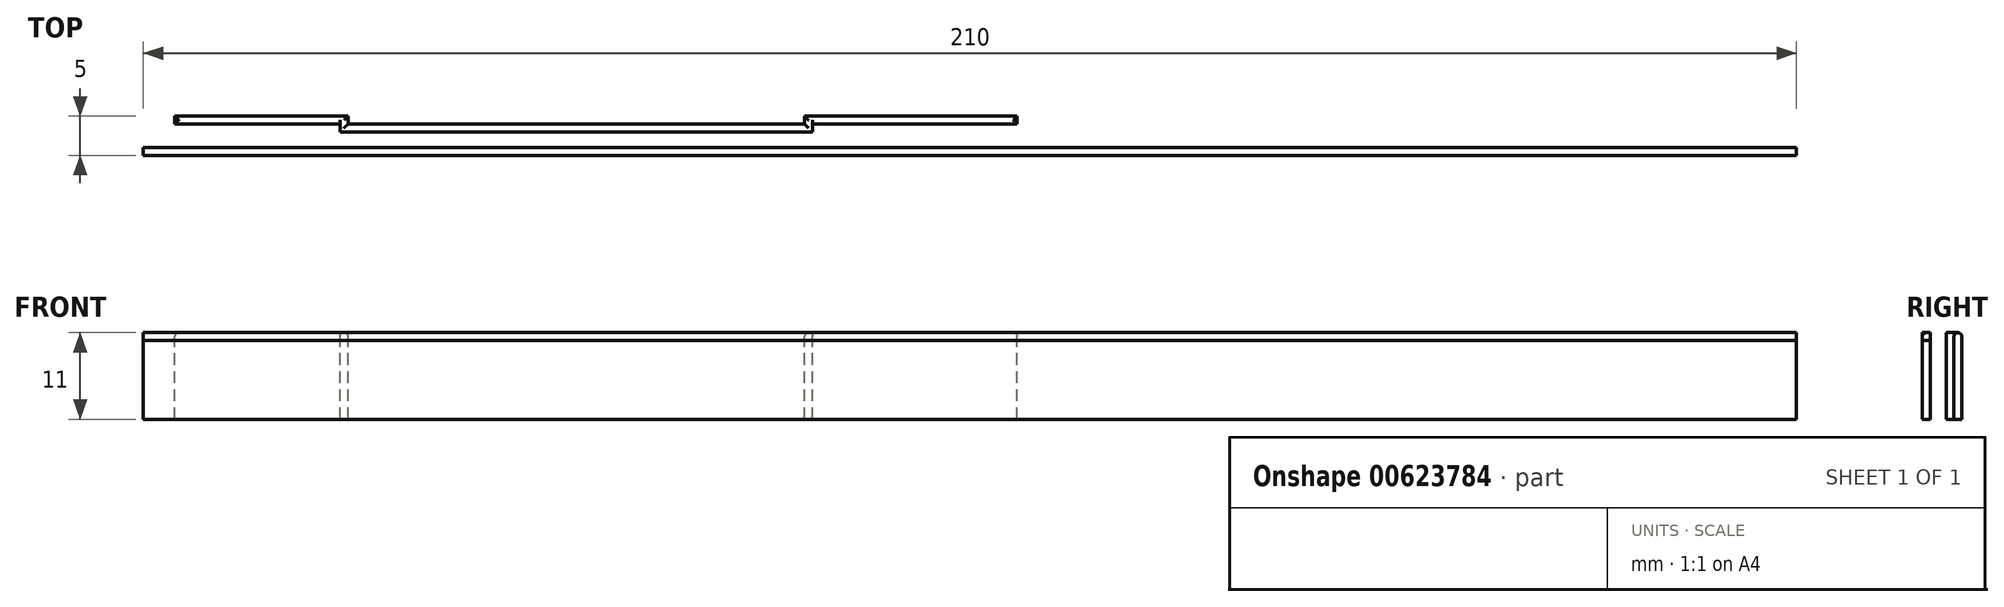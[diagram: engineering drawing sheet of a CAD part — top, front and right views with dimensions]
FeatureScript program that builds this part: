
annotation { "Feature Type Name" : "Feature", "Feature Type Description" : "" }
export const myFeature = defineFeature(function(context is Context, id is Id, definition is map)
    precondition{}
    {
        {
            var Q0;
            Q0=qCreatedBy(makeId("Top.planeOp"),FACE);
            var sketch = newSketch(context, id + "F0", { "sketchPlane" : qUnion([Q0])});
            skLineSegment(sketch, "E0.bottom", {"start": v(-105, -5) * mm, "end": v(105, -5) * mm});
            skLineSegment(sketch, "E0.top", {"start": v(-105, -9) * mm, "end": v(105, -9) * mm});
            skLineSegment(sketch, "E0.left", {"start": v(-105, -5) * mm, "end": v(-105, -9) * mm});
            skLineSegment(sketch, "E0.right", {"start": v(105, -5) * mm, "end": v(105, -9) * mm});
            skLineSegment(sketch, "E1", {"start": v(0, 0) * mm, "end": v(0, -5) * mm, "construction": true});
            skLineSegment(sketch, "E2", {"start": v(0, -5) * mm, "end": v(105, -5) * mm, "construction": true});
            skLineSegment(sketch, "E3.left", {"start": v(-105, -5) * mm, "end": v(-105, -5) * mm});
            skLineSegment(sketch, "E3.right", {"start": v(105, -5) * mm, "end": v(105, -5) * mm});
            skLineSegment(sketch, "E4.top", {"start": v(-105, -6) * mm, "end": v(105, -6) * mm});
            skLineSegment(sketch, "E4.left", {"start": v(-105, -5) * mm, "end": v(-105, -6) * mm});
            skLineSegment(sketch, "E4.right", {"start": v(105, -5) * mm, "end": v(105, -6) * mm});
            skLineSegment(sketch, "E5.top", {"start": v(-105, -8) * mm, "end": v(105, -8) * mm});
            skLineSegment(sketch, "E5.left", {"start": v(-105, -9) * mm, "end": v(-105, -8) * mm});
            skLineSegment(sketch, "E5.right", {"start": v(105, -9) * mm, "end": v(105, -8) * mm});
            skLineSegment(sketch, "E6", {"start": v(-105, -6) * mm, "end": v(-100, -6) * mm, "construction": true});
            skLineSegment(sketch, "E7", {"start": v(-100, -6) * mm, "end": v(-80, -6) * mm, "construction": true});
            skLineSegment(sketch, "E8", {"start": v(-80, -6) * mm, "end": v(-20, -6) * mm, "construction": true});
            skLineSegment(sketch, "E9", {"start": v(-20, -6) * mm, "end": v(5, -6) * mm, "construction": true});
            skLineSegment(sketch, "E10.bottom", {"start": v(-100, -6) * mm, "end": v(-80, -6) * mm});
            skLineSegment(sketch, "E10.top", {"start": v(-100, -5) * mm, "end": v(-80, -5) * mm});
            skLineSegment(sketch, "E10.left", {"start": v(-100, -6) * mm, "end": v(-100, -5) * mm});
            skLineSegment(sketch, "E10.right", {"start": v(-80, -6) * mm, "end": v(-80, -5) * mm});
            skLineSegment(sketch, "E11.bottom", {"start": v(-101, -5) * mm, "end": v(-79, -5) * mm});
            skLineSegment(sketch, "E11.top", {"start": v(-101, -4) * mm, "end": v(-79, -4) * mm});
            skLineSegment(sketch, "E11.left", {"start": v(-101, -5) * mm, "end": v(-101, -4) * mm});
            skLineSegment(sketch, "E11.right", {"start": v(-79, -5) * mm, "end": v(-79, -4) * mm});
            skLineSegment(sketch, "E12", {"start": v(-101, -5) * mm, "end": v(-100, -5) * mm});
            skLineSegment(sketch, "E13.bottom", {"start": v(-20, -6) * mm, "end": v(5, -6) * mm});
            skLineSegment(sketch, "E13.top", {"start": v(-20, -5) * mm, "end": v(5, -5) * mm});
            skLineSegment(sketch, "E13.left", {"start": v(-20, -6) * mm, "end": v(-20, -5) * mm});
            skLineSegment(sketch, "E13.right", {"start": v(5, -6) * mm, "end": v(5, -5) * mm});
            skLineSegment(sketch, "E14.bottom", {"start": v(-21, -5) * mm, "end": v(6, -5) * mm});
            skLineSegment(sketch, "E14.top", {"start": v(-21, -4) * mm, "end": v(6, -4) * mm});
            skLineSegment(sketch, "E14.left", {"start": v(-21, -5) * mm, "end": v(-21, -4) * mm});
            skLineSegment(sketch, "E14.right", {"start": v(6, -5) * mm, "end": v(6, -4) * mm});
            skLineSegment(sketch, "E15", {"start": v(-21, -5) * mm, "end": v(-20, -5) * mm, "construction": true});
            skSolve(sketch);
        }
        {
            var Q0;
            {var subQ4=sQuery(id+"F0.wireOp",EDGE,"E0.left");Q0=makeQuery(id+"F0.imprint","IMPRINT",FACE,{"disambiguationData":[TD([[makeQuery(id+"F0.imprint","IMPRINT",EDGE,{"derivedFrom":subQ4}),1.0]])]});}
            var Q1;
            Q1=makeQuery(id+"F0.imprint","IMPRINT",FACE,{"disambiguationData":[TD([[makeQuery(id+"F0.imprint","IMPRINT",EDGE,{"derivedFrom":sQuery(id+"F0.wireOp",EDGE,"E10.bottom")}),1.0]])]});
            var Q2;
            Q2=makeQuery(id+"F0.imprint","IMPRINT",FACE,{"disambiguationData":[TD([[makeQuery(id+"F0.imprint","IMPRINT",EDGE,{"derivedFrom":sQuery(id+"F0.wireOp",EDGE,"E13.bottom")}),1.0]])]});
            extrude(context, id + "F1", {"entities" : qUnion([Q0, Q1, Q2]), "oppositeDirection" : true, "depth" : 1 * mm, "offsetDistance" : 25 * mm});
        }
        {
            var Q0;
            Q0=makeQuery(id+"F0.imprint","IMPRINT",FACE,{"disambiguationData":[TD([[makeQuery(id+"F0.imprint","IMPRINT",EDGE,{"derivedFrom":sQuery(id+"F0.wireOp",EDGE,"E11.top")}),-1.0]])]});
            var Q1;
            {var subQ0=sQuery(id+"F0.wireOp",EDGE,"E4.left");Q1=makeQuery(id+"F0.imprint","IMPRINT",FACE,{"disambiguationData":[TD([[makeQuery(id+"F0.imprint","IMPRINT",EDGE,{"derivedFrom":subQ0}),1.0]])]});}
            var Q2;
            {var subQ0=sQuery(id+"F0.wireOp",EDGE,"E10.right");Q2=makeQuery(id+"F0.imprint","IMPRINT",FACE,{"disambiguationData":[TD([[makeQuery(id+"F0.imprint","IMPRINT",EDGE,{"derivedFrom":subQ0}),-1.0]])]});}
            var Q3;
            Q3=makeQuery(id+"F0.imprint","IMPRINT",FACE,{"disambiguationData":[TD([[makeQuery(id+"F0.imprint","IMPRINT",EDGE,{"derivedFrom":sQuery(id+"F0.wireOp",EDGE,"E0.top")}),1.0]])]});
            var Q4;
            Q4=makeQuery(id+"F0.imprint","IMPRINT",FACE,{"disambiguationData":[TD([[makeQuery(id+"F0.imprint","IMPRINT",EDGE,{"derivedFrom":sQuery(id+"F0.wireOp",EDGE,"E14.top")}),-1.0]])]});
            var Q5;
            {var subQ1=sQuery(id+"F0.wireOp",EDGE,"E4.right");Q5=makeQuery(id+"F0.imprint","IMPRINT",FACE,{"disambiguationData":[TD([[makeQuery(id+"F0.imprint","IMPRINT",EDGE,{"derivedFrom":subQ1}),-1.0]])]});}
            extrude(context, id + "F2", {"entities" : qUnion([Q0, Q1, Q2, Q3, Q4, Q5]), "oppositeDirection" : true, "depth" : 11 * mm, "offsetDistance" : 25 * mm});
        }
        {
            var Q0;
            {var subQ0=sQuery(id+"F0.wireOp",EDGE,"E0.bottom");Q0=makeQuery(id+"F2.opExtrude","CAP_EDGE",EDGE,{"disambiguationData":[OSD([subQ0]),TDD([makeQuery(id+"F0.imprint","IMPRINT",EDGE,{"disambiguationData":[TD([[makeQuery(id+"F0.imprint","INTERSECT",VERTEX,{"derivedFrom":[subQ0,sQuery(id+"F0.wireOp",EDGE,"E11.bottom"),sQuery(id+"F0.wireOp",EDGE,"E11.right")]}),-1.0]])],"derivedFrom":subQ0})])],"isStart":true});}
            var Q1;
            Q1=makeQuery(id+"F2.opExtrude","CAP_EDGE",EDGE,{"disambiguationData":[OSD([sQuery(id+"F0.wireOp",EDGE,"E14.left")])],"isStart":true});
            var Q2;
            Q2=makeQuery(id+"F2.opExtrude","CAP_EDGE",EDGE,{"disambiguationData":[OSD([sQuery(id+"F0.wireOp",EDGE,"E14.top")])],"isStart":true});
            var Q3;
            Q3=makeQuery(id+"F2.opExtrude","CAP_EDGE",EDGE,{"disambiguationData":[OSD([sQuery(id+"F0.wireOp",EDGE,"E0.top")])],"isStart":true});
            var Q4;
            Q4=makeQuery(id+"F2.opExtrude","CAP_EDGE",EDGE,{"disambiguationData":[OSD([sQuery(id+"F0.wireOp",EDGE,"E14.right")])],"isStart":true});
            var Q5;
            {var subQ0=sQuery(id+"F0.wireOp",EDGE,"E0.bottom");Q5=makeQuery(id+"F2.opExtrude","CAP_EDGE",EDGE,{"disambiguationData":[OSD([subQ0]),TDD([makeQuery(id+"F0.imprint","IMPRINT",EDGE,{"disambiguationData":[TD([[makeQuery(id+"F0.imprint","INTERSECT",VERTEX,{"derivedFrom":[subQ0,sQuery(id+"F0.wireOp",EDGE,"E4.right")]}),1.0]])],"derivedFrom":subQ0})])],"isStart":true});}
            var Q6;
            Q6=makeQuery(id+"F2.opExtrude","CAP_EDGE",EDGE,{"disambiguationData":[OSD([sQuery(id+"F0.wireOp",EDGE,"E11.top")])],"isStart":true});
            var Q7;
            Q7=makeQuery(id+"F2.opExtrude","CAP_EDGE",EDGE,{"disambiguationData":[OSD([sQuery(id+"F0.wireOp",EDGE,"E11.right")])],"isStart":true});
            var Q8;
            Q8=makeQuery(id+"F2.opExtrude","CAP_EDGE",EDGE,{"disambiguationData":[OSD([sQuery(id+"F0.wireOp",EDGE,"E11.left")])],"isStart":true});
            var Q9;
            {var subQ0=sQuery(id+"F0.wireOp",EDGE,"E0.bottom");Q9=makeQuery(id+"F2.opExtrude","CAP_EDGE",EDGE,{"disambiguationData":[OSD([subQ0]),TDD([makeQuery(id+"F0.imprint","IMPRINT",EDGE,{"disambiguationData":[TD([[makeQuery(id+"F0.imprint","INTERSECT",VERTEX,{"derivedFrom":[subQ0,sQuery(id+"F0.wireOp",EDGE,"E4.left")]}),-1.0]])],"derivedFrom":subQ0})])],"isStart":true});}
            fillet(context, id + "F3", {"entities" : qUnion([Q0, Q1, Q2, Q3, Q4, Q5, Q6, Q7, Q8, Q9]), "radius" : .5 * mm, "tangentPropagation" : true, "allowEdgeOverflow" : false});
        }
    });
